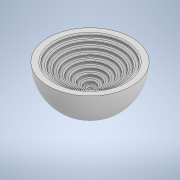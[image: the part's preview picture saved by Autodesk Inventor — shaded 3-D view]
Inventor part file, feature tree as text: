
AUTODESK INVENTOR PART (.ipt)
format: ipt  version: 2022 (Build 260153000, 153)  size: 442,368 bytes
history: native  units: mm
features: extrude x18, sketch x18, other x11, fillet x6
ambient origin geometry x8: Origin, YZ Plane, XZ Plane, XY Plane, X Axis, Y Axis, Z Axis, Center Point
bodies: Body1 (feature_tree)
feature tree (53):
  other  "實體1"
  extrude  "擠出1"  Depth=60.0mm
  fillet  "圓角1"  Radius=30.0mm
  extrude  "擠出2"  Depth=30.0mm
  extrude  "擠出3"  Depth=50.0mm
  extrude  "擠出4"  Depth=2.0mm TaperAngle=0.0deg
  extrude  "擠出5"  Depth=44.0mm
  extrude  "擠出6"  Depth=2.0mm TaperAngle=0.0deg
  extrude  "擠出7"  Depth=38.0mm
  extrude  "擠出8"  Depth=2.0mm TaperAngle=0.0deg
  extrude  "擠出9"  Depth=32.0mm
  extrude  "擠出11"  Depth=2.0mm TaperAngle=0.0deg
  extrude  "擠出12"  Depth=26.0mm
  extrude  "擠出13"  Depth=2.0mm TaperAngle=0.0deg
  extrude  "擠出16"  Depth=20.0mm
  fillet  "圓角2"  Radius=2.0mm
  extrude  "擠出17"  Depth=14.0mm
  fillet  "圓角3"  Radius=2.0mm
  extrude  "擠出18"  Depth=8.0mm
  fillet  "圓角4"  Radius=2.0mm
  extrude  "擠出19"  Depth=3.0mm
  fillet  "圓角5"  Radius=2.0mm
  other  "面圓角1"
  other  "面圓角2"
  other  "面圓角3"
  other  "面圓角4"
  other  "面圓角5"
  other  "面圓角6"
  other  "面圓角7"
  other  "面圓角8"
  extrude  "擠出20"  Depth=3.0mm
  other  "面圓角9"
  fillet  "圓角6"  Radius=50.0mm
  extrude  "擠出21"  Depth=3.0mm
  other  "面圓角10"
  sketch  "草圖3"
  sketch  "草圖4"
  sketch  "草圖5"
  sketch  "草圖6"
  sketch  "草圖7"
  sketch  "草圖8"
  sketch  "草圖9"
  sketch  "草圖10"
  sketch  "草圖11"
  sketch  "草圖14"
  sketch  "草圖15"
  sketch  "草圖16"
  sketch  "草圖25"
  sketch  "草圖26"
  sketch  "草圖27"
  sketch  "草圖29"
  sketch  "草圖30"
  sketch  "草圖31"
